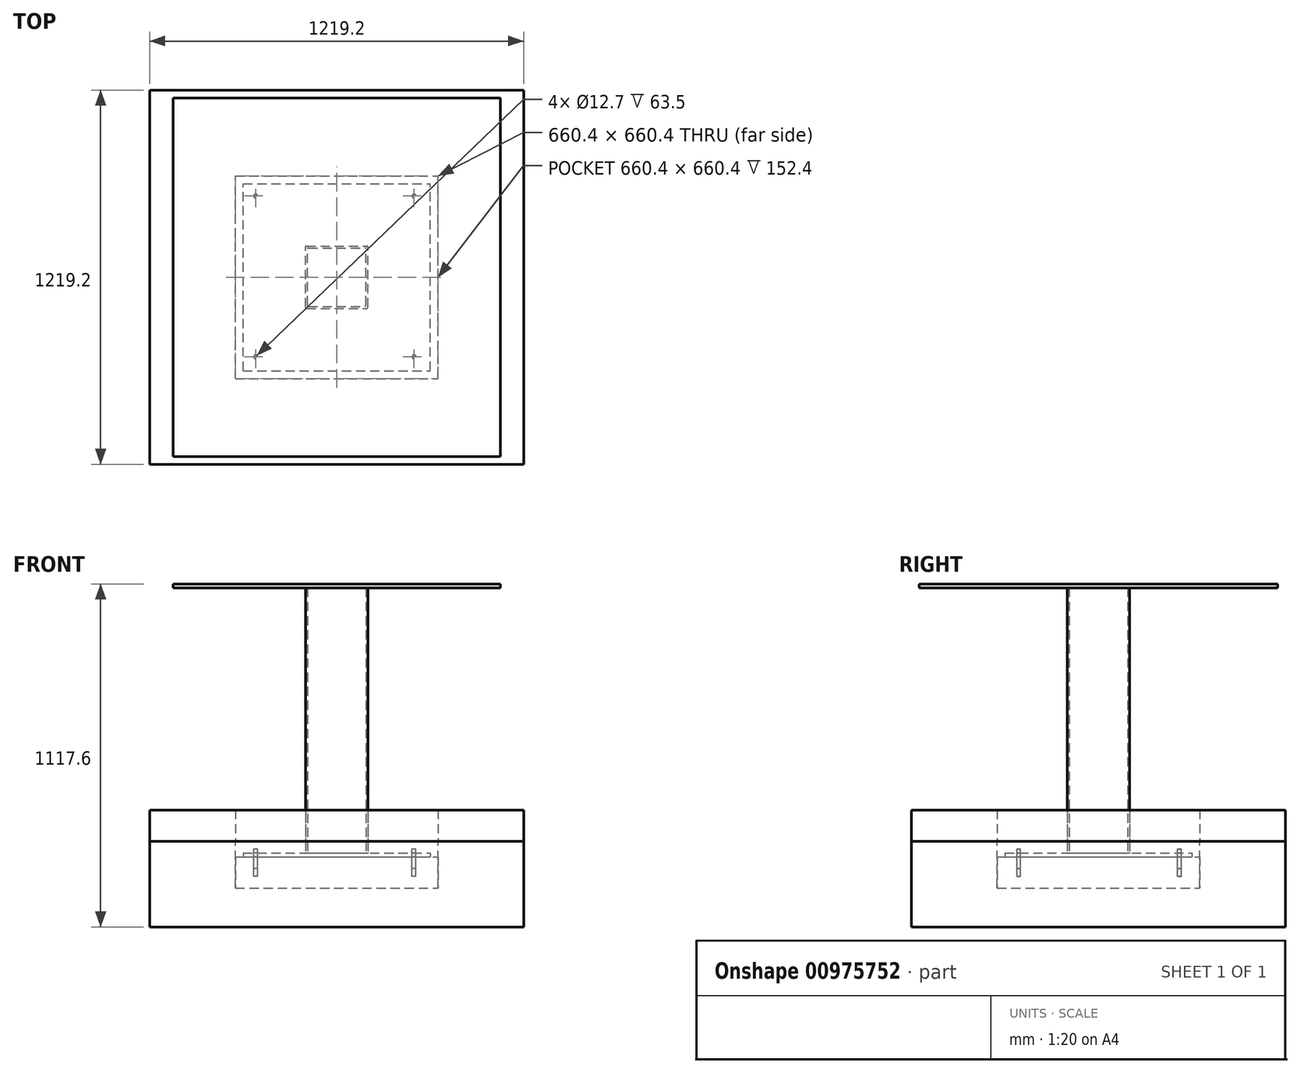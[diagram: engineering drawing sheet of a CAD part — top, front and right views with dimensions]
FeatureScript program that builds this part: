
annotation { "Feature Type Name" : "Feature", "Feature Type Description" : "" }
export const myFeature = defineFeature(function(context is Context, id is Id, definition is map)
    precondition{}
    {
        {
            var Q0;
            Q0=qCreatedBy(makeId("Top.planeOp"),FACE);
            var sketch = newSketch(context, id + "F0", { "sketchPlane" : qUnion([Q0])});
            skLineSegment(sketch, "E0.bottom", {"start": v(-609.6, -609.6) * mm, "end": v(609.6, -609.6) * mm});
            skLineSegment(sketch, "E0.top", {"start": v(-609.6, 609.6) * mm, "end": v(609.6, 609.6) * mm});
            skLineSegment(sketch, "E0.left", {"start": v(-609.6, -609.6) * mm, "end": v(-609.6, 609.6) * mm});
            skLineSegment(sketch, "E0.right", {"start": v(609.6, -609.6) * mm, "end": v(609.6, 609.6) * mm});
            skPoint(sketch, "E0.middle", {"position": v(0, 0) * mm});
            skSolve(sketch);
        }
        {
            var Q0;
            Q0 = qSketchRegion(id + "F0", true);
            extrude(context, id + "F1", {"entities" : qUnion([Q0]), "oppositeDirection" : true, "depth" : 304.8 * mm, "offsetDistance" : 25.4 * mm});
        }
        {
            var Q0;
            Q0=makeQuery(id+"F1.opExtrude","CAP_FACE",FACE,{"disambiguationData":[OSD([sQuery(id+"F0.wireOp",EDGE,"E0.bottom"),sQuery(id+"F0.wireOp",EDGE,"E0.top"),sQuery(id+"F0.wireOp",EDGE,"E0.left"),sQuery(id+"F0.wireOp",EDGE,"E0.right")])],"isStart":true});
            extrude(context, id + "F2", {"entities" : qUnion([Q0]), "operationType" : NewBodyOperationType.REMOVE, "oppositeDirection" : true, "depth" : 25.4 * mm, "offsetDistance" : 25.4 * mm});
        }
        {
            var Q0;
            Q0=makeQuery(id+"F2.boolean.opBoolean","COPY",FACE,{"derivedFrom":makeQuery(id+"F2.opExtrude","CAP_FACE",FACE,{"disambiguationData":[OSD([sQuery(id+"F0.wireOp",EDGE,"E0.bottom"),sQuery(id+"F0.wireOp",EDGE,"E0.top"),sQuery(id+"F0.wireOp",EDGE,"E0.left"),sQuery(id+"F0.wireOp",EDGE,"E0.right")])],"isStart":false})});
            var sketch = newSketch(context, id + "F3", { "sketchPlane" : qUnion([Q0])});
            skLineSegment(sketch, "E1.bottom", {"start": v(-330.2, -330.2) * mm, "end": v(330.2, -330.2) * mm});
            skLineSegment(sketch, "E1.top", {"start": v(-330.2, 330.2) * mm, "end": v(330.2, 330.2) * mm});
            skLineSegment(sketch, "E1.left", {"start": v(-330.2, -330.2) * mm, "end": v(-330.2, 330.2) * mm});
            skLineSegment(sketch, "E1.right", {"start": v(330.2, -330.2) * mm, "end": v(330.2, 330.2) * mm});
            skPoint(sketch, "E1.middle", {"position": v(0, 0) * mm});
            skSolve(sketch);
        }
        {
            var Q0;
            Q0=makeQuery(id+"F3.imprint","IMPRINT",FACE,{"disambiguationData":[TD([[makeQuery(id+"F3.imprint","IMPRINT",EDGE,{"derivedFrom":sQuery(id+"F3.wireOp",EDGE,"E1.bottom")}),1.0]])]});
            extrude(context, id + "F4", {"entities" : qUnion([Q0]), "operationType" : NewBodyOperationType.REMOVE, "oppositeDirection" : true, "depth" : 152.4 * mm, "offsetDistance" : 25.4 * mm});
        }
        {
            var Q0;
            Q0=makeQuery(id+"F4.boolean.opBoolean","COPY",FACE,{"derivedFrom":makeQuery(id+"F4.opExtrude","CAP_FACE",FACE,{"disambiguationData":[OSD([sQuery(id+"F3.wireOp",EDGE,"E1.bottom"),sQuery(id+"F3.wireOp",EDGE,"E1.top"),sQuery(id+"F3.wireOp",EDGE,"E1.left"),sQuery(id+"F3.wireOp",EDGE,"E1.right")])],"isStart":false})});
            var sketch = newSketch(context, id + "F5", { "sketchPlane" : qUnion([Q0])});
            skLineSegment(sketch, "E2.bottom", {"start": v(-330.2, -330.2) * mm, "end": v(330.2, -330.2) * mm});
            skLineSegment(sketch, "E2.top", {"start": v(-330.2, 330.2) * mm, "end": v(330.2, 330.2) * mm});
            skLineSegment(sketch, "E2.left", {"start": v(-330.2, -330.2) * mm, "end": v(-330.2, 330.2) * mm});
            skLineSegment(sketch, "E2.right", {"start": v(330.2, -330.2) * mm, "end": v(330.2, 330.2) * mm});
            skPoint(sketch, "E2.middle", {"position": v(0, 0) * mm});
            skSolve(sketch);
        }
        {
            var Q0;
            Q0 = qSketchRegion(id + "F5", true);
            extrude(context, id + "F6", {"entities" : qUnion([Q0]), "depth" : 101.6 * mm, "offsetDistance" : 25.4 * mm});
        }
        {
            var Q0;
            Q0=makeQuery(id+"F2.boolean.opBoolean","COPY",FACE,{"derivedFrom":makeQuery(id+"F2.opExtrude","CAP_FACE",FACE,{"disambiguationData":[OSD([sQuery(id+"F0.wireOp",EDGE,"E0.bottom"),sQuery(id+"F0.wireOp",EDGE,"E0.top"),sQuery(id+"F0.wireOp",EDGE,"E0.left"),sQuery(id+"F0.wireOp",EDGE,"E0.right")])],"isStart":false})});
            var sketch = newSketch(context, id + "F7", { "sketchPlane" : qUnion([Q0])});
            skLineSegment(sketch, "E3.0", {"start": v(-609.6, -609.6) * mm, "end": v(-609.6, 609.6) * mm});
            skLineSegment(sketch, "E3.1", {"start": v(-609.6, 609.6) * mm, "end": v(609.6, 609.6) * mm});
            skLineSegment(sketch, "E3.2", {"start": v(609.6, -609.6) * mm, "end": v(609.6, 609.6) * mm});
            skLineSegment(sketch, "E3.3", {"start": v(-609.6, -609.6) * mm, "end": v(609.6, -609.6) * mm});
            skLineSegment(sketch, "E4.0", {"start": v(-330.2, 330.2) * mm, "end": v(330.2, 330.2) * mm});
            skLineSegment(sketch, "E4.1", {"start": v(-330.2, -330.2) * mm, "end": v(-330.2, 330.2) * mm});
            skLineSegment(sketch, "E4.2", {"start": v(-330.2, -330.2) * mm, "end": v(330.2, -330.2) * mm});
            skLineSegment(sketch, "E4.3", {"start": v(330.2, -330.2) * mm, "end": v(330.2, 330.2) * mm});
            skSolve(sketch);
        }
        {
            var Q0;
            Q0 = qSketchRegion(id + "F7", true);
            extrude(context, id + "F8", {"entities" : qUnion([Q0]), "depth" : 101.6 * mm, "offsetDistance" : 25.4 * mm});
        }
        {
            var Q0;
            Q0=makeQuery(id+"F6.opExtrude","CAP_FACE",FACE,{"disambiguationData":[OSD([sQuery(id+"F5.wireOp",EDGE,"E2.bottom"),sQuery(id+"F5.wireOp",EDGE,"E2.top"),sQuery(id+"F5.wireOp",EDGE,"E2.left"),sQuery(id+"F5.wireOp",EDGE,"E2.right")])],"isStart":false});
            var sketch = newSketch(context, id + "F9", { "sketchPlane" : qUnion([Q0])});
            skLineSegment(sketch, "E5.bottom", {"start": v(-304.8, -304.8) * mm, "end": v(304.8, -304.8) * mm});
            skLineSegment(sketch, "E5.top", {"start": v(-304.8, 304.8) * mm, "end": v(304.8, 304.8) * mm});
            skLineSegment(sketch, "E5.left", {"start": v(-304.8, -304.8) * mm, "end": v(-304.8, 304.8) * mm});
            skLineSegment(sketch, "E5.right", {"start": v(304.8, -304.8) * mm, "end": v(304.8, 304.8) * mm});
            skPoint(sketch, "E5.middle", {"position": v(0, 0) * mm});
            skSolve(sketch);
        }
        {
            var Q0;
            Q0 = qSketchRegion(id + "F9", true);
            extrude(context, id + "F10", {"entities" : qUnion([Q0]), "depth" : 12.7 * mm, "offsetDistance" : 25.4 * mm});
        }
        {
            var Q0;
            Q0=makeQuery(id+"F10.opExtrude","CAP_FACE",FACE,{"disambiguationData":[OSD([sQuery(id+"F9.wireOp",EDGE,"E5.bottom"),sQuery(id+"F9.wireOp",EDGE,"E5.top"),sQuery(id+"F9.wireOp",EDGE,"E5.left"),sQuery(id+"F9.wireOp",EDGE,"E5.right")])],"isStart":false});
            var sketch = newSketch(context, id + "F11", { "sketchPlane" : qUnion([Q0])});
            skLineSegment(sketch, "E6.bottom", {"start": v(-98.43, -101.6) * mm, "end": v(98.43, -101.6) * mm});
            skLineSegment(sketch, "E6.top", {"start": v(-98.43, 101.6) * mm, "end": v(98.43, 101.6) * mm});
            skLineSegment(sketch, "E6.left", {"start": v(-101.6, -98.43) * mm, "end": v(-101.6, 98.43) * mm});
            skLineSegment(sketch, "E6.right", {"start": v(101.6, -98.43) * mm, "end": v(101.6, 98.43) * mm});
            skPoint(sketch, "E6.middle", {"position": v(0, 0) * mm});
            skLineSegment(sketch, "E7.0", {"start": v(-92.08, 95.25) * mm, "end": v(92.08, 95.25) * mm});
            skLineSegment(sketch, "E7.1", {"start": v(-95.25, -92.08) * mm, "end": v(-95.25, 92.08) * mm});
            skLineSegment(sketch, "E7.2", {"start": v(-92.08, -95.25) * mm, "end": v(92.08, -95.25) * mm});
            skLineSegment(sketch, "E7.3", {"start": v(95.25, -92.08) * mm, "end": v(95.25, 92.08) * mm});
            skPoint(sketch, "E8.visualSharp", {"position": v(-101.6, 101.6) * mm});
            skArc(sketch, "E8.filletArc", {"start": v(-98.43, 101.6) * mm, "mid": v(-100.67, 100.67) * mm, "end": v(-101.6, 98.43) * mm});
            skPoint(sketch, "E9.visualSharp", {"position": v(101.6, 101.6) * mm});
            skArc(sketch, "E9.filletArc", {"start": v(101.6, 98.43) * mm, "mid": v(100.67, 100.67) * mm, "end": v(98.43, 101.6) * mm});
            skPoint(sketch, "E10.visualSharp", {"position": v(95.25, 95.25) * mm});
            skArc(sketch, "E10.filletArc", {"start": v(95.25, 92.08) * mm, "mid": v(94.32, 94.32) * mm, "end": v(92.08, 95.25) * mm});
            skPoint(sketch, "E11.visualSharp", {"position": v(101.6, -101.6) * mm});
            skArc(sketch, "E11.filletArc", {"start": v(98.43, -101.6) * mm, "mid": v(100.67, -100.67) * mm, "end": v(101.6, -98.43) * mm});
            skPoint(sketch, "E12.visualSharp", {"position": v(95.25, -95.25) * mm});
            skArc(sketch, "E12.filletArc", {"start": v(92.08, -95.25) * mm, "mid": v(94.32, -94.32) * mm, "end": v(95.25, -92.08) * mm});
            skPoint(sketch, "E13.visualSharp", {"position": v(-101.6, -101.6) * mm});
            skArc(sketch, "E13.filletArc", {"start": v(-101.6, -98.43) * mm, "mid": v(-100.67, -100.67) * mm, "end": v(-98.43, -101.6) * mm});
            skPoint(sketch, "E14.visualSharp", {"position": v(-95.25, -95.25) * mm});
            skArc(sketch, "E14.filletArc", {"start": v(-95.25, -92.08) * mm, "mid": v(-94.32, -94.32) * mm, "end": v(-92.08, -95.25) * mm});
            skPoint(sketch, "E15.visualSharp", {"position": v(-95.25, 95.25) * mm});
            skArc(sketch, "E15.filletArc", {"start": v(-92.08, 95.25) * mm, "mid": v(-94.32, 94.32) * mm, "end": v(-95.25, 92.08) * mm});
            skSolve(sketch);
        }
        {
            var Q0;
            Q0 = qSketchRegion(id + "F11", true);
            extrude(context, id + "F12", {"entities" : qUnion([Q0]), "operationType" : NewBodyOperationType.ADD, "depth" : 863.6 * mm, "offsetDistance" : 25.4 * mm});
        }
        {
            var Q0;
            Q0=makeQuery(id+"F12.opExtrude","CAP_FACE",FACE,{"disambiguationData":[OSD([sQuery(id+"F11.wireOp",EDGE,"E6.bottom"),sQuery(id+"F11.wireOp",EDGE,"E6.top"),sQuery(id+"F11.wireOp",EDGE,"E6.left"),sQuery(id+"F11.wireOp",EDGE,"E6.right"),sQuery(id+"F11.wireOp",EDGE,"E7.0"),sQuery(id+"F11.wireOp",EDGE,"E7.1"),sQuery(id+"F11.wireOp",EDGE,"E7.2"),sQuery(id+"F11.wireOp",EDGE,"E7.3"),sQuery(id+"F11.wireOp",EDGE,"E8.filletArc"),sQuery(id+"F11.wireOp",EDGE,"E9.filletArc"),sQuery(id+"F11.wireOp",EDGE,"E10.filletArc"),sQuery(id+"F11.wireOp",EDGE,"E11.filletArc"),sQuery(id+"F11.wireOp",EDGE,"E12.filletArc"),sQuery(id+"F11.wireOp",EDGE,"E13.filletArc"),sQuery(id+"F11.wireOp",EDGE,"E14.filletArc"),sQuery(id+"F11.wireOp",EDGE,"E15.filletArc")])],"isStart":false});
            var sketch = newSketch(context, id + "F13", { "sketchPlane" : qUnion([Q0])});
            skLineSegment(sketch, "E16.bottom", {"start": v(-533.4, -584.2) * mm, "end": v(533.4, -584.2) * mm});
            skLineSegment(sketch, "E16.top", {"start": v(-533.4, 584.2) * mm, "end": v(533.4, 584.2) * mm});
            skLineSegment(sketch, "E16.left", {"start": v(-533.4, -584.2) * mm, "end": v(-533.4, 584.2) * mm});
            skLineSegment(sketch, "E16.right", {"start": v(533.4, -584.2) * mm, "end": v(533.4, 584.2) * mm});
            skPoint(sketch, "E16.middle", {"position": v(0, 0) * mm});
            skSolve(sketch);
        }
        {
            var Q0;
            Q0 = qSketchRegion(id + "F13", true);
            extrude(context, id + "F14", {"entities" : qUnion([Q0]), "operationType" : NewBodyOperationType.ADD, "depth" : 12.7 * mm, "offsetDistance" : 25.4 * mm});
        }
        {
            var Q0;
            {var subQ0=sQuery(id+"F9.wireOp",EDGE,"E5.left");var subQ1=sQuery(id+"F9.wireOp",EDGE,"E5.bottom");var subQ2=sQuery(id+"F9.wireOp",EDGE,"E5.right");var subQ3=sQuery(id+"F9.wireOp",EDGE,"E5.top");Q0=makeQuery(id+"F12.boolean.opBoolean","SPLIT",FACE,{"disambiguationData":[TD([makeQuery(id+"F10.opExtrude","SWEPT_FACE",FACE,{"disambiguationData":[OSD([subQ1])]})])],"derivedFrom":makeQuery(id+"F10.opExtrude","CAP_FACE",FACE,{"disambiguationData":[OSD([subQ1,subQ3,subQ0,subQ2])],"isStart":false})});}
            var sketch = newSketch(context, id + "F15", { "sketchPlane" : qUnion([Q0])});
            skCircle(sketch, "E17", {"center": v(-264.35, 264.35) * mm, "radius": 6.35 * mm});
            skCircle(sketch, "E18", {"center": v(252.23, 264.35) * mm, "radius": 6.35 * mm});
            skCircle(sketch, "E19", {"center": v(252.23, -259.8) * mm, "radius": 6.35 * mm});
            skCircle(sketch, "E20", {"center": v(-264.35, -259.8) * mm, "radius": 6.35 * mm});
            skSolve(sketch);
        }
        {
            var Q0;
            Q0 = qSketchRegion(id + "F15", true);
            extrude(context, id + "F16", {"entities" : qUnion([Q0]), "operationType" : NewBodyOperationType.REMOVE, "oppositeDirection" : true, "depth" : 76.2 * mm, "offsetDistance" : 25.4 * mm});
        }
        {
            var Q0;
            {var subQ0=sQuery(id+"F9.wireOp",EDGE,"E5.left");var subQ1=sQuery(id+"F9.wireOp",EDGE,"E5.bottom");var subQ2=sQuery(id+"F9.wireOp",EDGE,"E5.right");var subQ3=sQuery(id+"F9.wireOp",EDGE,"E5.top");Q0=makeQuery(id+"F12.boolean.opBoolean","SPLIT",FACE,{"disambiguationData":[TD([makeQuery(id+"F10.opExtrude","SWEPT_FACE",FACE,{"disambiguationData":[OSD([subQ1])]})])],"derivedFrom":makeQuery(id+"F10.opExtrude","CAP_FACE",FACE,{"disambiguationData":[OSD([subQ1,subQ3,subQ0,subQ2])],"isStart":false})});}
            var sketch = newSketch(context, id + "F17", { "sketchPlane" : qUnion([Q0])});
            skCircle(sketch, "E21.0", {"center": v(-264.35, 264.35) * mm, "radius": 6.35 * mm});
            skCircle(sketch, "E21.1", {"center": v(252.23, 264.35) * mm, "radius": 6.35 * mm});
            skCircle(sketch, "E21.2", {"center": v(252.23, -259.8) * mm, "radius": 6.35 * mm});
            skCircle(sketch, "E21.3", {"center": v(-264.35, -259.8) * mm, "radius": 6.35 * mm});
            skSolve(sketch);
        }
        {
            var Q0;
            Q0 = qSketchRegion(id + "F17", true);
            extrude(context, id + "F18", {"entities" : qUnion([Q0]), "oppositeDirection" : true, "depth" : 50.8 * mm, "offsetDistance" : 25.4 * mm, "hasSecondDirection" : true, "secondDirectionOppositeDirection" : false, "secondDirectionDepth" : 12.7 * mm});
        }
    });
